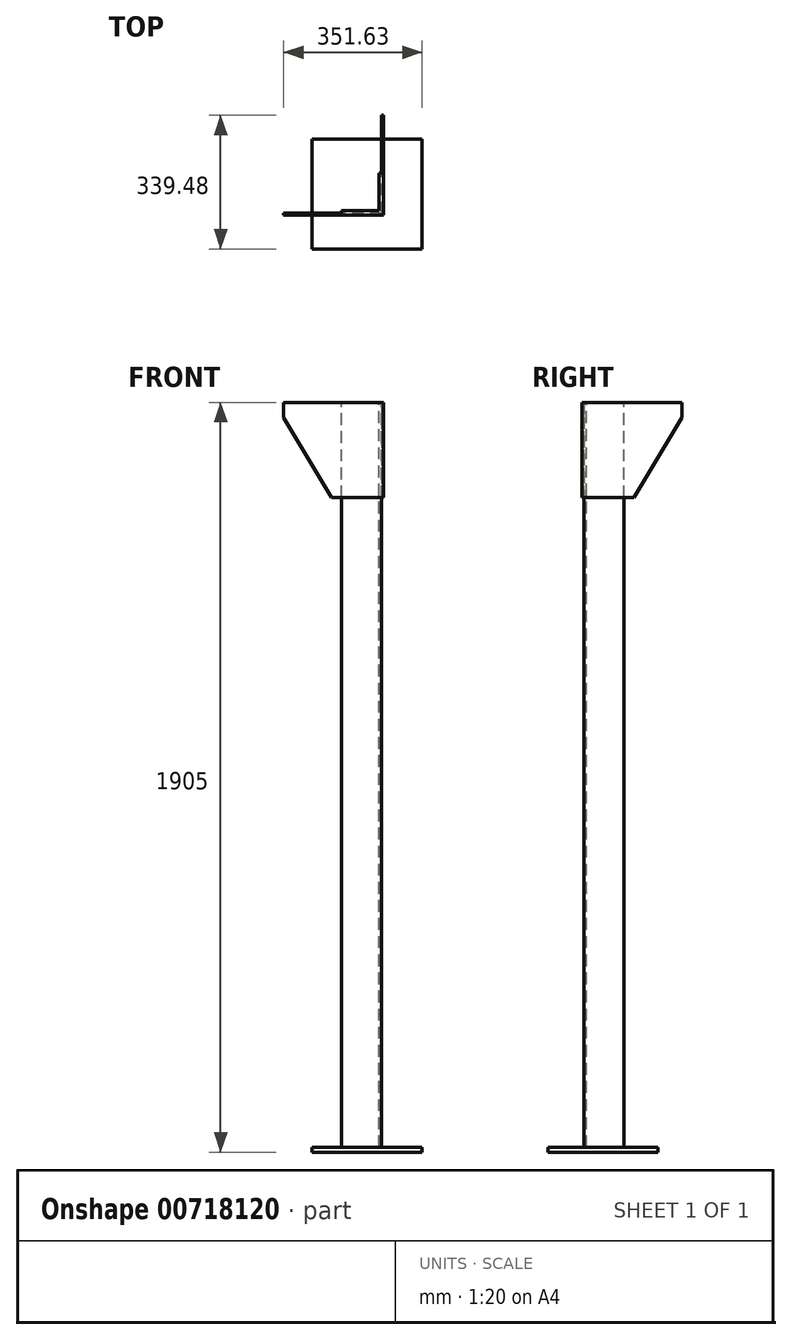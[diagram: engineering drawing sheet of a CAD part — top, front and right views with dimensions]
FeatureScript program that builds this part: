
annotation { "Feature Type Name" : "Feature", "Feature Type Description" : "" }
export const myFeature = defineFeature(function(context is Context, id is Id, definition is map)
    precondition{}
    {
        {
            var Q0;
            Q0=qCreatedBy(makeId("Top.planeOp"),FACE);
            var sketch = newSketch(context, id + "F0", { "sketchPlane" : qUnion([Q0])});
            skLineSegment(sketch, "E0", {"start": v(0, 0) * mm, "end": v(-254, 0) * mm});
            skLineSegment(sketch, "E1", {"start": v(0, 0) * mm, "end": v(0, 254) * mm});
            skLineSegment(sketch, "E2.0", {"start": v(-5.08, 5.08) * mm, "end": v(-254, 5.08) * mm});
            skLineSegment(sketch, "E2.1", {"start": v(-5.08, 5.08) * mm, "end": v(-5.08, 254) * mm});
            skLineSegment(sketch, "E3", {"start": v(-254, 0) * mm, "end": v(-254, 5.08) * mm});
            skLineSegment(sketch, "E4", {"start": v(-5.08, 254) * mm, "end": v(0, 254) * mm});
            skSolve(sketch);
        }
        {
            var Q0;
            Q0=makeQuery(id+"F0.imprint","IMPRINT",FACE,{"disambiguationData":[TD([[makeQuery(id+"F0.imprint","IMPRINT",EDGE,{"derivedFrom":sQuery(id+"F0.wireOp",EDGE,"E0")}),-1.0]])]});
            extrude(context, id + "F1", {"entities" : qUnion([Q0]), "depth" : 38.1 * mm, "offsetDistance" : 25.4 * mm});
        }
        {
            var Q0;
            Q0=qCreatedBy(makeId("Top.planeOp"),FACE);
            cPlane(context, id + "F2", {"entities" : qUnion([Q0]), "cplaneType" : CPlaneType.OFFSET, "offset" : 203.2 * mm, "oppositeDirection" : true, "width" : 152.4 * mm, "height" : 152.4 * mm});
        }
        {
            var Q0;
            Q0=qCreatedBy(id+"F2.planeOp",FACE);
            var sketch = newSketch(context, id + "F3", { "sketchPlane" : qUnion([Q0])});
            skLineSegment(sketch, "E5", {"start": v(0, 0) * mm, "end": v(0, 132.08) * mm});
            skLineSegment(sketch, "E6", {"start": v(0, 0) * mm, "end": v(-132.08, 0) * mm});
            skLineSegment(sketch, "E7.0", {"start": v(-5.08, 5.08) * mm, "end": v(-5.08, 132.08) * mm});
            skLineSegment(sketch, "E7.1", {"start": v(-5.08, 5.08) * mm, "end": v(-132.08, 5.08) * mm});
            skLineSegment(sketch, "E8", {"start": v(-132.08, 0) * mm, "end": v(-132.08, 5.08) * mm});
            skLineSegment(sketch, "E9", {"start": v(-5.08, 132.08) * mm, "end": v(0, 132.08) * mm});
            skSolve(sketch);
        }
        {
            var Q1;
            Q1=makeQuery(id+"F1.opExtrude","CAP_FACE",FACE,{"disambiguationData":[OSD([sQuery(id+"F0.wireOp",EDGE,"E0"),sQuery(id+"F0.wireOp",EDGE,"E1"),sQuery(id+"F0.wireOp",EDGE,"E2.0"),sQuery(id+"F0.wireOp",EDGE,"E2.1"),sQuery(id+"F0.wireOp",EDGE,"E3"),sQuery(id+"F0.wireOp",EDGE,"E4")])],"isStart":true});
            var Q2;
            Q2=makeQuery(id+"F3.imprint","IMPRINT",FACE,{"disambiguationData":[TD([[makeQuery(id+"F3.imprint","IMPRINT",EDGE,{"derivedFrom":sQuery(id+"F3.wireOp",EDGE,"E5")}),1.0]])]});
            loft(context, id + "F4", {"operationType" : NewBodyOperationType.ADD, "sheetProfilesArray" : [{ "sheetProfileEntities" : qUnion([Q1]) }, { "sheetProfileEntities" : qUnion([Q2]) }]});
        }
        {
            var Q0;
            Q0=makeQuery(id+"F1.opExtrude","CAP_FACE",FACE,{"disambiguationData":[OSD([sQuery(id+"F0.wireOp",EDGE,"E0"),sQuery(id+"F0.wireOp",EDGE,"E1"),sQuery(id+"F0.wireOp",EDGE,"E2.0"),sQuery(id+"F0.wireOp",EDGE,"E2.1"),sQuery(id+"F0.wireOp",EDGE,"E3"),sQuery(id+"F0.wireOp",EDGE,"E4")])],"isStart":false});
            var sketch = newSketch(context, id + "F5", { "sketchPlane" : qUnion([Q0])});
            skLineSegment(sketch, "E10", {"start": v(-5.08, 5.08) * mm, "end": v(-5.08, 106.68) * mm});
            skLineSegment(sketch, "E11", {"start": v(-5.08, 5.08) * mm, "end": v(-106.68, 5.08) * mm});
            skLineSegment(sketch, "E12.0", {"start": v(-11.43, 11.43) * mm, "end": v(-106.68, 11.43) * mm});
            skLineSegment(sketch, "E12.1", {"start": v(-11.43, 11.43) * mm, "end": v(-11.43, 106.68) * mm});
            skLineSegment(sketch, "E13", {"start": v(-5.08, 106.68) * mm, "end": v(-11.43, 106.68) * mm});
            skLineSegment(sketch, "E14", {"start": v(-106.68, 11.43) * mm, "end": v(-106.68, 5.08) * mm});
            skSolve(sketch);
        }
        {
            var Q0;
            Q0=makeQuery(id+"F5.imprint","IMPRINT",FACE,{"disambiguationData":[TD([[makeQuery(id+"F5.imprint","IMPRINT",EDGE,{"derivedFrom":sQuery(id+"F5.wireOp",EDGE,"E10")}),1.0]])]});
            extrude(context, id + "F6", {"entities" : qUnion([Q0]), "operationType" : NewBodyOperationType.ADD, "oppositeDirection" : true, "depth" : 1905 * mm, "offsetDistance" : 25.4 * mm});
        }
        {
            var Q0;
            Q0=makeQuery(id+"F6.opExtrude","CAP_FACE",FACE,{"disambiguationData":[OSD([sQuery(id+"F5.wireOp",EDGE,"E10"),sQuery(id+"F5.wireOp",EDGE,"E11"),sQuery(id+"F5.wireOp",EDGE,"E12.0"),sQuery(id+"F5.wireOp",EDGE,"E12.1"),sQuery(id+"F5.wireOp",EDGE,"E13"),sQuery(id+"F5.wireOp",EDGE,"E14")])],"isStart":false});
            var sketch = newSketch(context, id + "F7", { "sketchPlane" : qUnion([Q0])});
            skPoint(sketch, "E15.middle", {"position": v(-11.43, -11.43) * mm});
            skPoint(sketch, "E16", {"position": v(-42.07, -54.22) * mm});
            skLineSegment(sketch, "E17.bottom", {"start": v(-181.77, 85.48) * mm, "end": v(97.63, 85.48) * mm});
            skLineSegment(sketch, "E17.top", {"start": v(-181.77, -193.92) * mm, "end": v(97.63, -193.92) * mm});
            skLineSegment(sketch, "E17.left", {"start": v(-181.77, 85.48) * mm, "end": v(-181.77, -193.92) * mm});
            skLineSegment(sketch, "E17.right", {"start": v(97.63, 85.48) * mm, "end": v(97.63, -193.92) * mm});
            skSolve(sketch);
        }
        {
            var Q0;
            Q0 = qSketchRegion(id + "F7", true);
            extrude(context, id + "F8", {"entities" : qUnion([Q0]), "operationType" : NewBodyOperationType.ADD, "oppositeDirection" : true, "depth" : 12.7 * mm, "offsetDistance" : 25.4 * mm});
        }
    });
